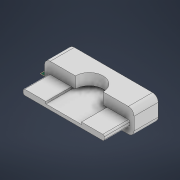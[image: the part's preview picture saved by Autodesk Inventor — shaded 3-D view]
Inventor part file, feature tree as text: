
AUTODESK INVENTOR PART (.ipt)
format: ipt  version: 2022 (Build 260153000, 153)  size: 477,184 bytes
history: native  units: mm
features: sketch x7, extrude x6, fillet x2, emboss x1, plane x1
ambient origin geometry x8: Origin, YZ Plane, XZ Plane, XY Plane, X Axis, Y Axis, Z Axis, Center Point
bodies: Solid1 (feature_tree)
feature tree (17):
  extrude  "Extrusion1"  Depth=17.0mm
  extrude  "20 mL cross"  Depth=8.0mm TaperAngle=0.0deg
  extrude  "20 mL top"  Depth=8.0mm TaperAngle=0.0deg
  extrude  "Extrusion4"  Depth=63.0mm
  emboss  "Emboss1"
  plane  "Work Plane1"
  extrude  "Extrusion8"  Depth=1.0mm
  extrude  "Extrusion10"  Depth=5.2mm
  fillet  "Fillet5"  Radius=18.0mm
  fillet  "Fillet6"  Radius=5.2mm
  sketch  "Sketch1"  dims[d0=63.0mm d1=17.0mm]
  sketch  "Sketch2"  dims[d2=35.0mm d3=0.0mm d5=8.0mm d6=0.0mm]
  sketch  "Sketch3"  dims[d8=1.5mm d9=0.0mm d11=8.0mm d12=0.0mm]
  sketch  "Sketch4"  dims[d19=63.0mm d20=18.0mm]
  sketch  "Sketch10"  dims[d33=1.0mm d34=0.0mm d36=18.0mm]
  sketch  "Sketch11"  dims[d37=19.5mm d40=25.0mm d41=18.0mm d42=5.2mm d43=0.0mm]
  sketch  "Sketch13"  dims[d52=3.0mm d53=3.0mm d54=18.0mm d55=0.0mm d64=1.0mm d65=4.0mm d51=0.5mm]
